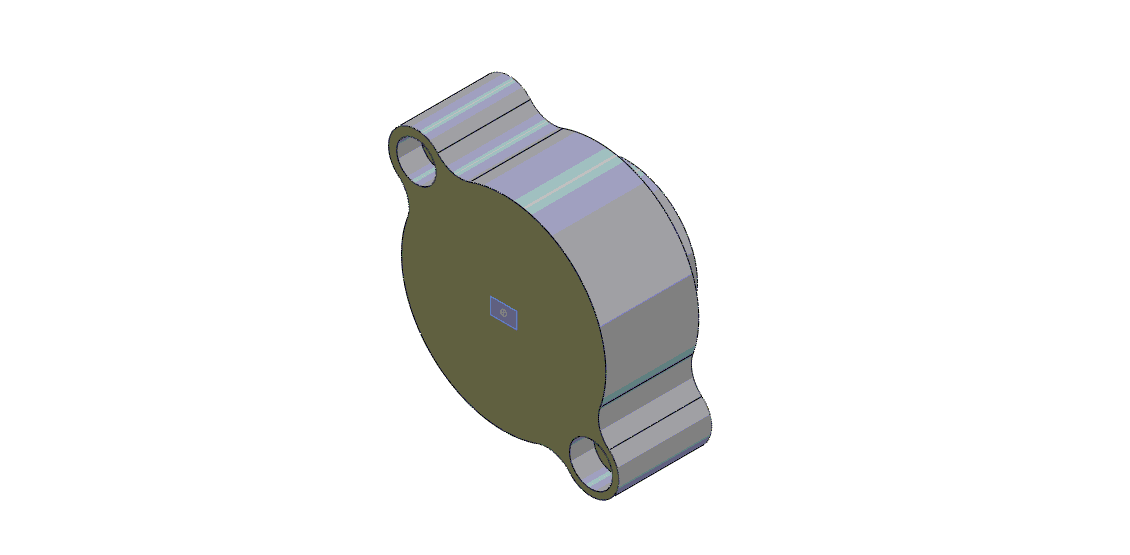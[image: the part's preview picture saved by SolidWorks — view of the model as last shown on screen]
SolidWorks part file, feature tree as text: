
SOLIDWORKS PART (.sldprt)
format: sldprt  version: not decoded by parser v0  size: 200,704 bytes
history: native  units: mm
features: sketch x7, plane x4, extrude x2, hole x2, material x1 (+10 scaffold rows collapsed)
feature tree (26):
  scaffold x10  (default folders/planes/origin — collapsed)
  material  "Matériau <non spécifié>"
  plane  "FRONT"
  plane  "TOP"
  plane  "RIGHT"
  plane  "Plan1"  Offset=838.2mm
  sketch  "Esquisse1"
  extrude  "Boss.-Extru.1"  Depth=635mm
  sketch  "Esquisse2"  dims[D1=972.82mm]
  extrude  "Boss.-Extru.2"  Depth=203.2mm
  sketch  "Esquisse3"  dims[D1=40.0mm]
  hole  "Perçage1"  Diameter=139.7mm Depth=838.2mm
  sketch  "Esquisse6"
  sketch  "Esquisse5"  dims[Diamètre=139.7mm Profondeur=838.2mm Diamètre chambrage=266.7mm Profondeur chambrage=165.1mm]
  hole  "Perçage2"  Diameter=139.7mm Depth=838.2mm
  sketch  "Esquisse8"
  sketch  "Esquisse7"  dims[Diamètre=139.7mm Profondeur=838.2mm Diamètre chambrage=292.1mm Profondeur chambrage=165.1mm]
decode coverage: 8 of 11 modeling features carry decoded parameters
note: suppression state not decoded; provenance and decode notes live in map.json
